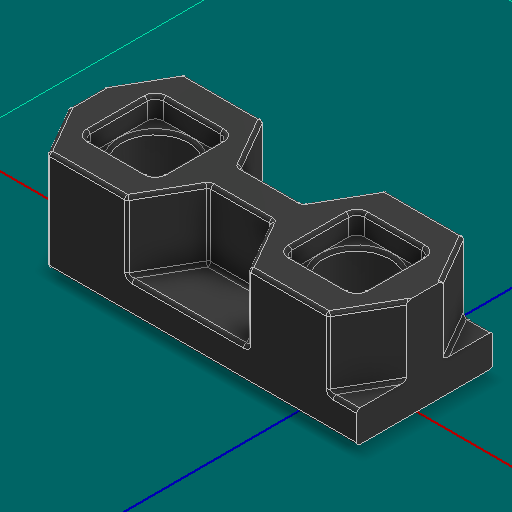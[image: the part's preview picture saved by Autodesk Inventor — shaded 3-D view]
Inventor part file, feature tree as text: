
AUTODESK INVENTOR PART (.ipt)
format: ipt  version: 2025 (Build 290162000, 162)  size: 397,824 bytes
history: native  units: in
note: dims shown in document units (in); Inventor stores cm internally (conversion verified against a paired STEP export)
features: other x3, sketch x2
ambient origin geometry x8: Origin, YZ Plane, XZ Plane, XY Plane, X Axis, Y Axis, Z Axis, Center Point
bodies: Solid1 (feature_tree)
feature tree (5):
  other  "Bearing Flat Low Profile 2-Hole.ipt"
  other  "Solid1::Bearing Flat Low Profile 2-Hole.ipt"
  other  "TaggingFeature1"
  sketch  "Sketch1"  dims[d0=0.3937in]
  sketch  "Sketch2"
